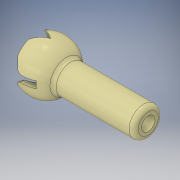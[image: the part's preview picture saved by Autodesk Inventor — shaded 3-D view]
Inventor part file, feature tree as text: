
AUTODESK INVENTOR PART (.ipt)
format: ipt  version: 2016 (Build 200138000, 138)  size: 339,968 bytes
history: native  units: in
note: dims shown in document units (in); Inventor stores cm internally (conversion verified against a paired STEP export)
features: sketch x12, extrude x7, plane x5, other x2, fillet x2, chamfer x2, revolve x1, loft x1, pattern_circular x1
ambient origin geometry x8: Origin, YZ Plane, XZ Plane, XY Plane, X Axis, Y Axis, Z Axis, Center Point
bodies: Solid1 (feature_tree)
feature tree (33):
  plane  "Work Plane1"
  extrude  "OUter Shell"  TaperAngle=90.0deg  [1 undecoded]
  revolve  "Revolution2"  [1 undecoded]
  plane  "Work Plane8"
  other  "Inner Shell"
  plane  "Work Plane9"
  extrude  "Oval Expansion"  Depth=0.4375in
  sketch  "Sketch8"  dims[d21=0.51in d29=0.226in]
  plane  "Work Plane15"
  extrude  "Extrusion4"  Depth=0.236in
  extrude  "Extrusion6"  Depth=0.226in
  plane  "Work Plane12"
  sketch  "Sketch13"  dims[d42=0.0in d43=90.0deg d44=0.0in d45=90.0deg d46=0.2in]
  loft  "Loft2"
  sketch  "Sketch14"  dims[d47=0.5in d48=0.0in d50=0.5in d51=0.0in]
  extrude  "Extrusion7"  Depth=0.226in
  extrude  "Extrusion8"  Depth=0.2in
  sketch  "Sketch17"  dims[d57=0.88in]
  sketch  "Sketch18"  dims[d60=0.6318in]
  extrude  "Extrusion10"  Depth=0.5in TaperAngle=0.0deg
  pattern_circular  "Circular Pattern1"  Angle=30.0deg  [1 undecoded]
  fillet  "Fillet1"  Radius=1.0in
  fillet  "Fillet2"  Radius=1.5748in
  chamfer  "Chamfer1"  Distance=0.1in
  chamfer  "Chamfer2"  Distance=0.08in
  sketch  "Sketch2"  dims[d2=1.757in d3=0.0in d4=90.0deg]
  sketch  "Sketch3"  dims[d11=-0.125in d12=0.7508in]
  sketch  "Sketch5"  dims[d13=90.0deg d17=0.4375in]
  sketch  "Sketch7"  dims[d18=1.0in d19=0.0in d20=0.236in]
  sketch  "Sketch10"  dims[d30=0.15in d31=0.0in d37=0.088in d38=0.0in]
  sketch  "Sketch12"  dims[d39=0.3in d41=0.226in]
  other  "Edges1"
  sketch  "Sketch19"  dims[d65=30.0deg d66=30.0deg d67=1.0in d68=0.0in d69=1.5748in d70=360.0deg d72=0.1in d73=0.08in d74=0.05in d75=0.125in d76=45.0deg d77=0.1in d78=0.125in d79=45.0deg]
note: 3 required parameter values undecoded (feature->parameter linkage not recoverable at this tier; creation-order binding heuristic only, values carry confidence <= 0.55)